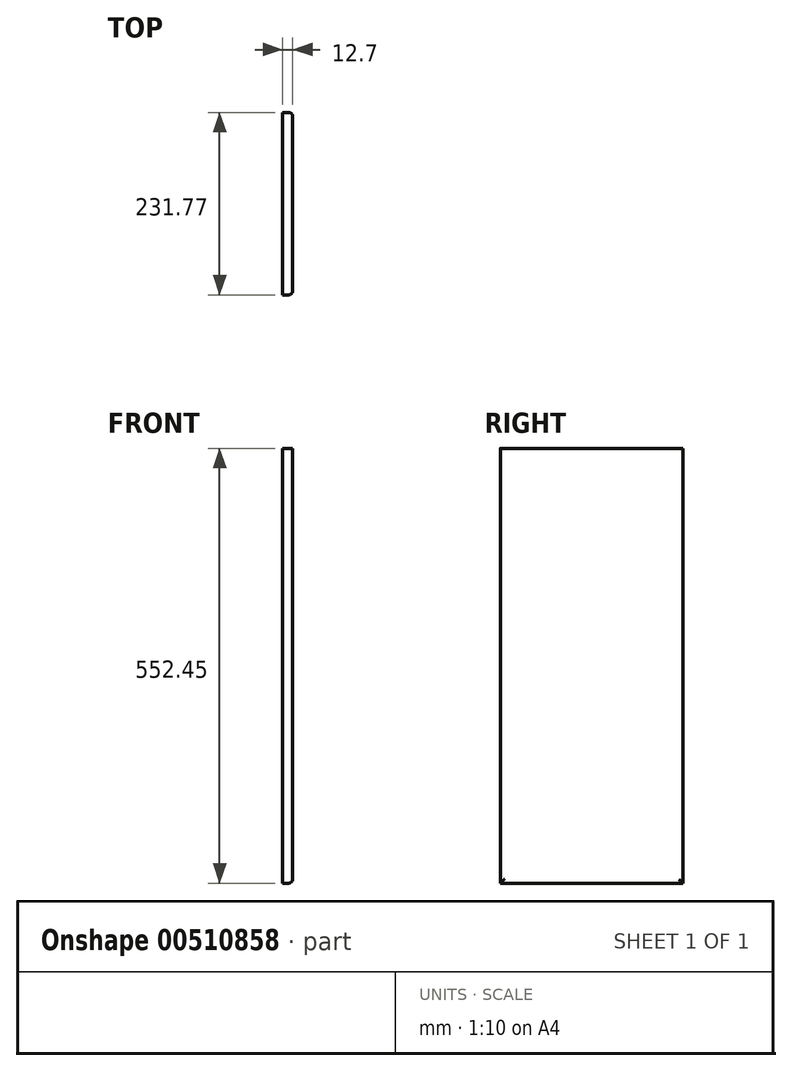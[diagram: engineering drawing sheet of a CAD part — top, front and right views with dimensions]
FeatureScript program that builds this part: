
annotation { "Feature Type Name" : "Feature", "Feature Type Description" : "" }
export const myFeature = defineFeature(function(context is Context, id is Id, definition is map)
    precondition{}
    {
        {
            var Q0;
            Q0=qCreatedBy(makeId("Top.planeOp"),FACE);
            var sketch = newSketch(context, id + "F0", { "sketchPlane" : qUnion([Q0])});
            skLineSegment(sketch, "E0.bottom", {"start": v(3.96, -7.71) * mm, "end": v(-8.74, -7.71) * mm});
            skLineSegment(sketch, "E0.top", {"start": v(3.96, 224.06) * mm, "end": v(-8.74, 224.06) * mm});
            skLineSegment(sketch, "E0.left", {"start": v(3.96, -7.71) * mm, "end": v(3.96, 224.06) * mm});
            skLineSegment(sketch, "E0.right", {"start": v(-8.74, -7.71) * mm, "end": v(-8.74, 224.06) * mm});
            skSolve(sketch);
        }
        {
            var Q0;
            Q0=makeQuery(id+"F0.imprint","IMPRINT",FACE,{"disambiguationData":[TD([[makeQuery(id+"F0.imprint","IMPRINT",EDGE,{"derivedFrom":sQuery(id+"F0.wireOp",EDGE,"E0.bottom")}),-1.0]])]});
            extrude(context, id + "F1", {"entities" : qUnion([Q0]), "depth" : 552.45 * mm, "offsetDistance" : 25.4 * mm});
        }
        {
            var Q0;
            Q0=makeQuery(id+"F1.opExtrude","SWEPT_EDGE",EDGE,{"disambiguationData":[OSD([sQuery(id+"F0.wireOp",EDGE,"E0.bottom"),sQuery(id+"F0.wireOp",EDGE,"E0.left")])]});
            var Q1;
            Q1=makeQuery(id+"F1.opExtrude","SWEPT_EDGE",EDGE,{"disambiguationData":[OSD([sQuery(id+"F0.wireOp",EDGE,"E0.top"),sQuery(id+"F0.wireOp",EDGE,"E0.left")])]});
            var Q2;
            Q2=makeQuery(id+"F1.opExtrude","CAP_EDGE",EDGE,{"disambiguationData":[OSD([sQuery(id+"F0.wireOp",EDGE,"E0.left")])],"isStart":true});
            fillet(context, id + "F2", {"entities" : qUnion([Q0, Q1, Q2]), "radius" : 5.08 * mm, "tangentPropagation" : true, "allowEdgeOverflow" : false});
        }
    });
